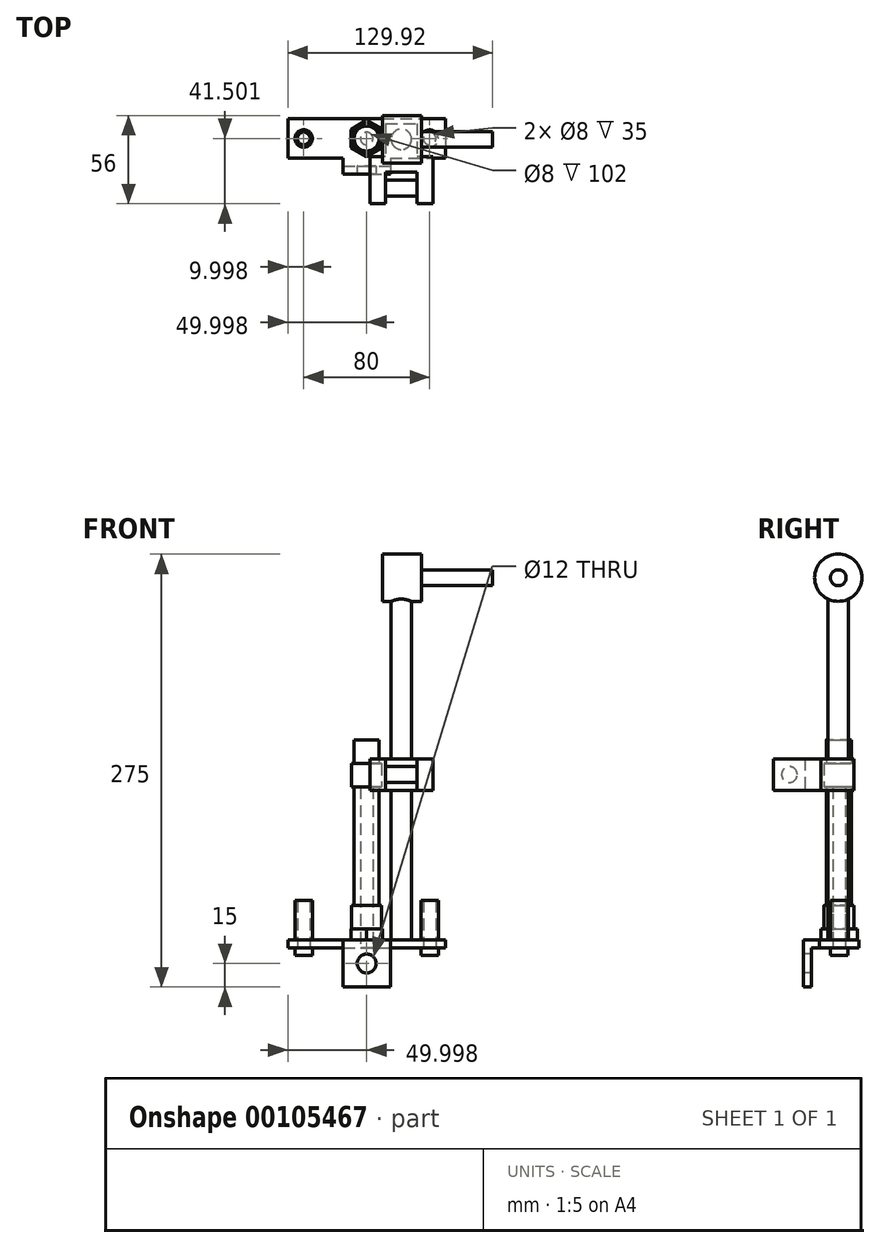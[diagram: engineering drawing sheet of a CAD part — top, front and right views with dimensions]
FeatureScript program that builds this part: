
annotation { "Feature Type Name" : "Feature", "Feature Type Description" : "" }
export const myFeature = defineFeature(function(context is Context, id is Id, definition is map)
    precondition{}
    {
        {
            var Q0;
            Q0=qCreatedBy(makeId("Top.planeOp"),FACE);
            var sketch = newSketch(context, id + "F0", { "sketchPlane" : qUnion([Q0])});
            skLineSegment(sketch, "E0.bottom", {"start": v(-27.42, 13) * mm, "end": v(72.58, 13) * mm});
            skLineSegment(sketch, "E0.top", {"start": v(-27.42, -12) * mm, "end": v(7.58, -12) * mm});
            skLineSegment(sketch, "E0.left", {"start": v(-27.42, 13) * mm, "end": v(-27.42, -12) * mm});
            skLineSegment(sketch, "E0.right", {"start": v(72.58, 13) * mm, "end": v(72.58, -12) * mm});
            skLineSegment(sketch, "E1.top", {"start": v(7.58, -22) * mm, "end": v(37.58, -22) * mm});
            skLineSegment(sketch, "E1.left", {"start": v(7.58, -12) * mm, "end": v(7.58, -22) * mm});
            skLineSegment(sketch, "E1.right", {"start": v(37.58, -12) * mm, "end": v(37.58, -22) * mm});
            skCircle(sketch, "E2", {"center": v(22.58, 0.5) * mm, "radius": 4 * mm});
            skCircle(sketch, "E3", {"center": v(-17.42, 0.5) * mm, "radius": 4 * mm});
            skCircle(sketch, "E4.MirrorC", {"center": v(62.58, 0.5) * mm, "radius": 4 * mm});
            skLineSegment(sketch, "E5.trimOffspring", {"start": v(37.58, -12) * mm, "end": v(72.58, -12) * mm});
            skSolve(sketch);
        }
        {
            var Q0;
            Q0 = qSketchRegion(id + "F0", true);
            extrude(context, id + "F1", {"entities" : qUnion([Q0]), "depth" : 5 * mm});
        }
        {
            var Q0;
            Q0=makeQuery(id+"F1.opExtrude","CAP_FACE",FACE,{"disambiguationData":[OSD([sQuery(id+"F0.wireOp",EDGE,"E0.bottom"),sQuery(id+"F0.wireOp",EDGE,"E0.top"),sQuery(id+"F0.wireOp",EDGE,"E0.left"),sQuery(id+"F0.wireOp",EDGE,"E0.right"),sQuery(id+"F0.wireOp",EDGE,"E1.top"),sQuery(id+"F0.wireOp",EDGE,"E1.left"),sQuery(id+"F0.wireOp",EDGE,"E1.right"),sQuery(id+"F0.wireOp",EDGE,"E2"),sQuery(id+"F0.wireOp",EDGE,"E3"),sQuery(id+"F0.wireOp",EDGE,"E4.MirrorC"),sQuery(id+"F0.wireOp",EDGE,"E5.trimOffspring")])],"isStart":false});
            var sketch = newSketch(context, id + "F2", { "sketchPlane" : qUnion([Q0])});
            skCircle(sketch, "E6", {"center": v(-17.42, 0.5) * mm, "radius": 4 * mm});
            skCircle(sketch, "E7", {"center": v(-17.42, 0.5) * mm, "radius": 5.5 * mm});
            skCircle(sketch, "E8", {"center": v(62.58, 0.5) * mm, "radius": 4 * mm});
            skCircle(sketch, "E9", {"center": v(62.58, 0.5) * mm, "radius": 5.5 * mm});
            skSolve(sketch);
        }
        {
            var Q0;
            Q0 = qSketchRegion(id + "F2", true);
            extrude(context, id + "F3", {"entities" : qUnion([Q0]), "operationType" : NewBodyOperationType.ADD, "depth" : 25 * mm});
        }
        {
            var Q0;
            Q0 = qSketchRegion(id + "F2", true);
            extrude(context, id + "F4", {"entities" : qUnion([Q0]), "operationType" : NewBodyOperationType.ADD, "oppositeDirection" : true, "depth" : 10 * mm});
        }
        {
            var Q0;
            Q0=makeQuery(id+"F1.opExtrude","CAP_FACE",FACE,{"disambiguationData":[OSD([sQuery(id+"F0.wireOp",EDGE,"E0.bottom"),sQuery(id+"F0.wireOp",EDGE,"E0.top"),sQuery(id+"F0.wireOp",EDGE,"E0.left"),sQuery(id+"F0.wireOp",EDGE,"E0.right"),sQuery(id+"F0.wireOp",EDGE,"E1.top"),sQuery(id+"F0.wireOp",EDGE,"E1.left"),sQuery(id+"F0.wireOp",EDGE,"E1.right"),sQuery(id+"F0.wireOp",EDGE,"E2"),sQuery(id+"F0.wireOp",EDGE,"E3"),sQuery(id+"F0.wireOp",EDGE,"E4.MirrorC"),sQuery(id+"F0.wireOp",EDGE,"E5.trimOffspring")])],"isStart":true});
            var sketch = newSketch(context, id + "F5", { "sketchPlane" : qUnion([Q0])});
            skLineSegment(sketch, "E10.bottom", {"start": v(7.58, 22) * mm, "end": v(37.58, 22) * mm});
            skLineSegment(sketch, "E10.top", {"start": v(7.58, 17) * mm, "end": v(37.58, 17) * mm});
            skLineSegment(sketch, "E10.left", {"start": v(7.58, 22) * mm, "end": v(7.58, 17) * mm});
            skLineSegment(sketch, "E10.right", {"start": v(37.58, 22) * mm, "end": v(37.58, 17) * mm});
            skSolve(sketch);
        }
        {
            var Q0;
            Q0 = qSketchRegion(id + "F5", true);
            extrude(context, id + "F6", {"entities" : qUnion([Q0]), "operationType" : NewBodyOperationType.ADD, "depth" : 25 * mm});
        }
        {
            var Q0;
            Q0=makeQuery(id+"F1.opExtrude","CAP_FACE",FACE,{"disambiguationData":[OSD([sQuery(id+"F0.wireOp",EDGE,"E0.bottom"),sQuery(id+"F0.wireOp",EDGE,"E0.top"),sQuery(id+"F0.wireOp",EDGE,"E0.left"),sQuery(id+"F0.wireOp",EDGE,"E0.right"),sQuery(id+"F0.wireOp",EDGE,"E1.top"),sQuery(id+"F0.wireOp",EDGE,"E1.left"),sQuery(id+"F0.wireOp",EDGE,"E1.right"),sQuery(id+"F0.wireOp",EDGE,"E2"),sQuery(id+"F0.wireOp",EDGE,"E3"),sQuery(id+"F0.wireOp",EDGE,"E4.MirrorC"),sQuery(id+"F0.wireOp",EDGE,"E5.trimOffspring")])],"isStart":false});
            var sketch = newSketch(context, id + "F7", { "sketchPlane" : qUnion([Q0])});
            skCircle(sketch, "E11", {"center": v(22.58, 0.5) * mm, "radius": 4 * mm});
            skCircle(sketch, "E12.cCircle", {"center": v(22.58, 0.5) * mm, "radius": 10 * mm, "construction": true});
            skLineSegment(sketch, "E12.0", {"start": v(12.58, -5.27) * mm, "end": v(12.58, 6.27) * mm});
            skLineSegment(sketch, "E12.1", {"start": v(12.58, 6.27) * mm, "end": v(22.58, 12.05) * mm});
            skLineSegment(sketch, "E12.2", {"start": v(22.58, 12.05) * mm, "end": v(32.58, 6.27) * mm});
            skLineSegment(sketch, "E12.3", {"start": v(32.58, 6.27) * mm, "end": v(32.58, -5.27) * mm});
            skLineSegment(sketch, "E12.4", {"start": v(32.58, -5.27) * mm, "end": v(22.58, -11.05) * mm});
            skLineSegment(sketch, "E12.5", {"start": v(22.58, -11.05) * mm, "end": v(12.58, -5.27) * mm});
            skPoint(sketch, "E12.0.midPoint", {"position": v(12.58, 0.5) * mm});
            skSolve(sketch);
        }
        {
            var Q0;
            Q0 = qSketchRegion(id + "F7", true);
            extrude(context, id + "F8", {"entities" : qUnion([Q0]), "operationType" : NewBodyOperationType.ADD, "depth" : 7 * mm});
        }
        {
            var Q0;
            Q0=makeQuery(id+"F8.opExtrude","CAP_FACE",FACE,{"disambiguationData":[OSD([sQuery(id+"F7.wireOp",EDGE,"E11"),sQuery(id+"F7.wireOp",EDGE,"E12.0"),sQuery(id+"F7.wireOp",EDGE,"E12.1"),sQuery(id+"F7.wireOp",EDGE,"E12.2"),sQuery(id+"F7.wireOp",EDGE,"E12.3"),sQuery(id+"F7.wireOp",EDGE,"E12.4"),sQuery(id+"F7.wireOp",EDGE,"E12.5")])],"isStart":false});
            var sketch = newSketch(context, id + "F9", { "sketchPlane" : qUnion([Q0])});
            skCircle(sketch, "E13", {"center": v(22.58, 0.5) * mm, "radius": 9.5 * mm});
            skCircle(sketch, "E14", {"center": v(22.58, 0.5) * mm, "radius": 4 * mm});
            skSolve(sketch);
        }
        {
            var Q0;
            Q0 = qSketchRegion(id + "F9", true);
            extrude(context, id + "F10", {"entities" : qUnion([Q0]), "operationType" : NewBodyOperationType.ADD, "depth" : 15 * mm});
        }
        {
            var Q0;
            Q0=makeQuery(id+"F10.opExtrude","CAP_FACE",FACE,{"disambiguationData":[OSD([sQuery(id+"F9.wireOp",EDGE,"E13"),sQuery(id+"F9.wireOp",EDGE,"E14")])],"isStart":false});
            var sketch = newSketch(context, id + "F11", { "sketchPlane" : qUnion([Q0])});
            skCircle(sketch, "E15", {"center": v(22.58, 0.5) * mm, "radius": 4 * mm});
            skCircle(sketch, "E16", {"center": v(22.58, 0.5) * mm, "radius": 8 * mm});
            skSolve(sketch);
        }
        {
            var Q0;
            Q0 = qSketchRegion(id + "F11", true);
            extrude(context, id + "F12", {"entities" : qUnion([Q0]), "operationType" : NewBodyOperationType.ADD, "depth" : 75 * mm});
        }
        {
            var Q0;
            Q0=makeQuery(id+"F12.opExtrude","CAP_FACE",FACE,{"disambiguationData":[OSD([sQuery(id+"F11.wireOp",EDGE,"E15"),sQuery(id+"F11.wireOp",EDGE,"E16")])],"isStart":false});
            var sketch = newSketch(context, id + "F13", { "sketchPlane" : qUnion([Q0])});
            skCircle(sketch, "E17", {"center": v(22.58, 0.5) * mm, "radius": 9.5 * mm});
            skSolve(sketch);
        }
        {
            var Q0;
            Q0 = qSketchRegion(id + "F13", true);
            extrude(context, id + "F14", {"entities" : qUnion([Q0]), "operationType" : NewBodyOperationType.ADD, "depth" : 15 * mm});
        }
        {
            var Q0;
            Q0=makeQuery(id+"F14.opExtrude","CAP_FACE",FACE,{"disambiguationData":[OSD([sQuery(id+"F13.wireOp",EDGE,"E17")])],"isStart":false});
            var sketch = newSketch(context, id + "F15", { "sketchPlane" : qUnion([Q0])});
            skCircle(sketch, "E18", {"center": v(22.58, 0.5) * mm, "radius": 8 * mm});
            skSolve(sketch);
        }
        {
            var Q0;
            Q0 = qSketchRegion(id + "F15", true);
            extrude(context, id + "F16", {"entities" : qUnion([Q0]), "operationType" : NewBodyOperationType.ADD, "depth" : 15 * mm});
        }
        {
            var Q0;
            Q0=makeQuery(id+"F1.opExtrude","CAP_FACE",FACE,{"disambiguationData":[OSD([sQuery(id+"F0.wireOp",EDGE,"E0.bottom"),sQuery(id+"F0.wireOp",EDGE,"E0.top"),sQuery(id+"F0.wireOp",EDGE,"E0.left"),sQuery(id+"F0.wireOp",EDGE,"E0.right"),sQuery(id+"F0.wireOp",EDGE,"E1.top"),sQuery(id+"F0.wireOp",EDGE,"E1.left"),sQuery(id+"F0.wireOp",EDGE,"E1.right"),sQuery(id+"F0.wireOp",EDGE,"E2"),sQuery(id+"F0.wireOp",EDGE,"E3"),sQuery(id+"F0.wireOp",EDGE,"E4.MirrorC"),sQuery(id+"F0.wireOp",EDGE,"E5.trimOffspring")])],"isStart":false});
            var sketch = newSketch(context, id + "F17", { "sketchPlane" : qUnion([Q0])});
            skCircle(sketch, "E19", {"center": v(44.58, 0) * mm, "radius": 6.5 * mm});
            skSolve(sketch);
        }
        {
            var Q0;
            Q0=makeQuery(id+"F17.imprint","IMPRINT",FACE,{"disambiguationData":[TD([[makeQuery(id+"F17.imprint","IMPRINT",EDGE,{"derivedFrom":sQuery(id+"F17.wireOp",EDGE,"E19")}),1.0]])]});
            extrude(context, id + "F18", {"entities" : qUnion([Q0]), "operationType" : NewBodyOperationType.ADD, "depth" : 240 * mm});
        }
        {
            var Q0;
            Q0=qCreatedBy(makeId("Top.planeOp"),FACE);
            cPlane(context, id + "F19", {"entities" : qUnion([Q0]), "cplaneType" : CPlaneType.OFFSET, "offset" : 110 * mm, "width" : 150 * mm, "height" : 150 * mm});
        }
        {
            var Q0;
            Q0=qCreatedBy(id+"F19.planeOp",FACE);
            var sketch = newSketch(context, id + "F20", { "sketchPlane" : qUnion([Q0])});
            skLineSegment(sketch, "E20.bottom", {"start": v(34.58, 10) * mm, "end": v(54.58, 10) * mm});
            skLineSegment(sketch, "E20.top", {"start": v(34.58, -11) * mm, "end": v(54.58, -11) * mm});
            skLineSegment(sketch, "E20.left", {"start": v(34.58, 10) * mm, "end": v(34.58, -11) * mm});
            skLineSegment(sketch, "E20.right", {"start": v(54.58, 10) * mm, "end": v(54.58, -11) * mm});
            skSolve(sketch);
        }
        {
            var Q0;
            Q0 = qSketchRegion(id + "F20", true);
            extrude(context, id + "F21", {"entities" : qUnion([Q0]), "operationType" : NewBodyOperationType.ADD, "endBound" : BoundingType.SYMMETRIC, "depth" : 20 * mm});
        }
        {
            var Q0;
            Q0=qCreatedBy(makeId("Right.planeOp"),FACE);
            cPlane(context, id + "F22", {"entities" : qUnion([Q0]), "cplaneType" : CPlaneType.OFFSET, "offset" : 45 * mm, "width" : 150 * mm, "height" : 150 * mm});
        }
        {
            var Q0;
            Q0=qCreatedBy(id+"F22.planeOp",FACE);
            var sketch = newSketch(context, id + "F23", { "sketchPlane" : qUnion([Q0])});
            skCircle(sketch, "E21", {"center": v(0, 235) * mm, "radius": 15 * mm});
            skSolve(sketch);
        }
        {
            var Q0;
            Q0=makeQuery(id+"F23.imprint","IMPRINT",FACE,{"disambiguationData":[TD([[makeQuery(id+"F23.imprint","IMPRINT",EDGE,{"derivedFrom":sQuery(id+"F23.wireOp",EDGE,"E21")}),1.0]])]});
            extrude(context, id + "F24", {"entities" : qUnion([Q0]), "operationType" : NewBodyOperationType.ADD, "endBound" : BoundingType.SYMMETRIC, "depth" : 25 * mm});
        }
        {
            var Q0;
            Q0=makeQuery(id+"F24.opExtrude","CAP_FACE",FACE,{"disambiguationData":[OSD([sQuery(id+"F23.wireOp",EDGE,"E21")])],"isStart":true});
            var sketch = newSketch(context, id + "F25", { "sketchPlane" : qUnion([Q0])});
            skCircle(sketch, "E22", {"center": v(0, 235) * mm, "radius": 5 * mm});
            skSolve(sketch);
        }
        {
            var Q0;
            Q0 = qSketchRegion(id + "F25", true);
            extrude(context, id + "F26", {"entities" : qUnion([Q0]), "operationType" : NewBodyOperationType.ADD, "oppositeDirection" : true, "depth" : 70 * mm});
        }
        {
            var Q0;
            Q0=makeQuery(id+"F6.boolean.opBoolean","MERGE",FACE,{"derivedFrom":[makeQuery(id+"F1.opExtrude","SWEPT_FACE",FACE,{"disambiguationData":[OSD([sQuery(id+"F0.wireOp",EDGE,"E1.top")])]}),makeQuery(id+"F6.opExtrude","SWEPT_FACE",FACE,{"disambiguationData":[OSD([sQuery(id+"F5.wireOp",EDGE,"E10.bottom")])]})]});
            var sketch = newSketch(context, id + "F27", { "sketchPlane" : qUnion([Q0])});
            skPoint(sketch, "E23.centerSnap0", {"position": v(37.58, -10) * mm});
            skPoint(sketch, "E23.centerSnap1", {"position": v(22.58, -25) * mm});
            skCircle(sketch, "E24", {"center": v(22.58, -10) * mm, "radius": 6 * mm});
            skSolve(sketch);
        }
        {
            var Q0;
            Q0 = qSketchRegion(id + "F27", true);
            extrude(context, id + "F28", {"entities" : qUnion([Q0]), "operationType" : NewBodyOperationType.REMOVE, "oppositeDirection" : true, "depth" : 25 * mm});
        }
        {
            var Q0;
            Q0=makeQuery(id+"F21.opExtrude","SWEPT_FACE",FACE,{"disambiguationData":[OSD([sQuery(id+"F20.wireOp",EDGE,"E20.right")])]});
            cPlane(context, id + "F29", {"entities" : qUnion([Q0]), "cplaneType" : CPlaneType.OFFSET, "offset" : 10 * mm, "oppositeDirection" : true, "width" : 150 * mm, "height" : 150 * mm});
        }
        {
            var Q0;
            Q0=makeQuery(id+"F21.opExtrude","SWEPT_FACE",FACE,{"disambiguationData":[OSD([sQuery(id+"F20.wireOp",EDGE,"E20.top")])]});
            var sketch = newSketch(context, id + "F30", { "sketchPlane" : qUnion([Q0])});
            skLineSegment(sketch, "E25.bottom", {"start": v(64.58, 100) * mm, "end": v(24.58, 100) * mm});
            skLineSegment(sketch, "E25.top", {"start": v(64.58, 120) * mm, "end": v(24.58, 120) * mm});
            skLineSegment(sketch, "E25.left", {"start": v(64.58, 100) * mm, "end": v(64.58, 120) * mm});
            skLineSegment(sketch, "E25.right", {"start": v(24.58, 100) * mm, "end": v(24.58, 120) * mm});
            skPoint(sketch, "E25.middle", {"position": v(44.58, 110) * mm});
            skPoint(sketch, "E25.middle.positionSnap0", {"position": v(44.58, 120) * mm});
            skPoint(sketch, "E25.middle.positionSnap1", {"position": v(54.58, 110) * mm});
            skPoint(sketch, "E25.centerSnap0", {"position": v(44.58, 120) * mm});
            skPoint(sketch, "E25.centerSnap1", {"position": v(54.58, 110) * mm});
            skSolve(sketch);
        }
        {
            var Q0;
            Q0 = qSketchRegion(id + "F30", true);
            extrude(context, id + "F31", {"entities" : qUnion([Q0]), "operationType" : NewBodyOperationType.ADD, "depth" : 10 * mm});
        }
        {
            var Q0;
            Q0=makeQuery(id+"F31.opExtrude","CAP_FACE",FACE,{"disambiguationData":[OSD([sQuery(id+"F30.wireOp",EDGE,"E25.bottom"),sQuery(id+"F30.wireOp",EDGE,"E25.top"),sQuery(id+"F30.wireOp",EDGE,"E25.left"),sQuery(id+"F30.wireOp",EDGE,"E25.right")])],"isStart":false});
            var sketch = newSketch(context, id + "F32", { "sketchPlane" : qUnion([Q0])});
            skLineSegment(sketch, "E26.bottom", {"start": v(64.58, 120) * mm, "end": v(54.58, 120) * mm});
            skLineSegment(sketch, "E26.top", {"start": v(64.58, 100) * mm, "end": v(54.58, 100) * mm});
            skLineSegment(sketch, "E26.left", {"start": v(64.58, 120) * mm, "end": v(64.58, 100) * mm});
            skLineSegment(sketch, "E26.right", {"start": v(54.58, 120) * mm, "end": v(54.58, 100) * mm});
            skLineSegment(sketch, "E27.bottom", {"start": v(24.58, 120) * mm, "end": v(34.58, 120) * mm});
            skLineSegment(sketch, "E27.top", {"start": v(24.58, 100) * mm, "end": v(34.58, 100) * mm});
            skLineSegment(sketch, "E27.left", {"start": v(24.58, 120) * mm, "end": v(24.58, 100) * mm});
            skLineSegment(sketch, "E27.right", {"start": v(34.58, 120) * mm, "end": v(34.58, 100) * mm});
            skSolve(sketch);
        }
        {
            var Q0;
            Q0 = qSketchRegion(id + "F32", true);
            extrude(context, id + "F33", {"entities" : qUnion([Q0]), "operationType" : NewBodyOperationType.ADD, "depth" : 20 * mm});
        }
        {
            var Q0;
            Q0=makeQuery(id+"F33.opExtrude","SWEPT_FACE",FACE,{"disambiguationData":[OSD([sQuery(id+"F32.wireOp",EDGE,"E26.right")])]});
            var sketch = newSketch(context, id + "F34", { "sketchPlane" : qUnion([Q0])});
            skCircle(sketch, "E28", {"center": v(31, 110) * mm, "radius": 5 * mm});
            skPoint(sketch, "E28.centerSnap0", {"position": v(41, 110) * mm});
            skSolve(sketch);
        }
        {
            var Q0;
            Q0 = qSketchRegion(id + "F34", true);
            var Q1;
            Q1=makeQuery(id+"F34.imprint","IMPRINT",FACE,{"disambiguationData":[TD([[makeQuery(id+"F34.imprint","IMPRINT",EDGE,{"derivedFrom":sQuery(id+"F34.wireOp",EDGE,"E28")}),1.0]])]});
            var Q2;
            Q2=makeQuery(id+"F33.opExtrude","SWEPT_FACE",FACE,{"disambiguationData":[OSD([sQuery(id+"F32.wireOp",EDGE,"E27.right")])]});
            extrude(context, id + "F35", {"entities" : qUnion([Q0, Q1]), "operationType" : NewBodyOperationType.ADD, "endBound" : BoundingType.UP_TO_SURFACE, "endBoundEntityFace" : qUnion([Q2]), "depth" : 25 * mm});
        }
    });
